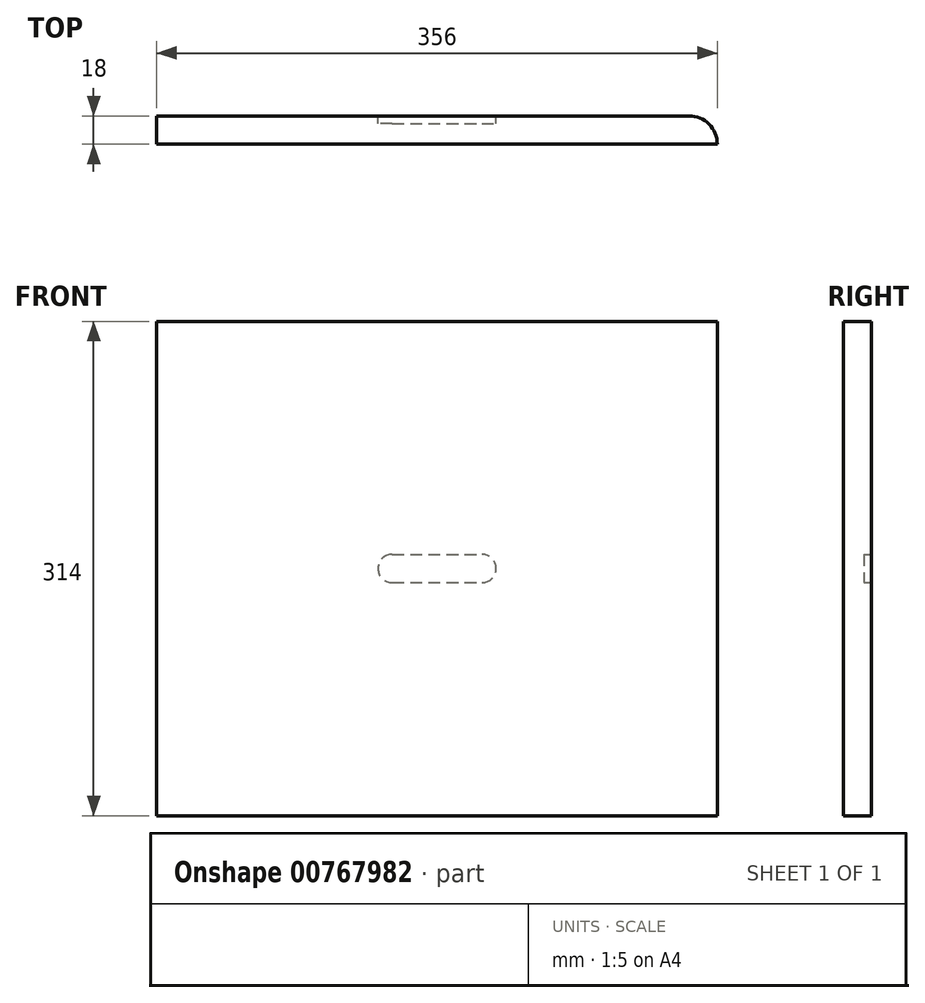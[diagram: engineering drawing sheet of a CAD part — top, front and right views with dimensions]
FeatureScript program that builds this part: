
annotation { "Feature Type Name" : "Feature", "Feature Type Description" : "" }
export const myFeature = defineFeature(function(context is Context, id is Id, definition is map)
    precondition{}
    {
        {
            var Q0;
            Q0=qCreatedBy(makeId("Front.planeOp"),FACE);
            var sketch = newSketch(context, id + "F0", { "sketchPlane" : qUnion([Q0])});
            skLineSegment(sketch, "E0.bottom", {"start": v(178, 157) * mm, "end": v(-178, 157) * mm});
            skLineSegment(sketch, "E0.top", {"start": v(178, -157) * mm, "end": v(-178, -157) * mm});
            skLineSegment(sketch, "E0.left", {"start": v(178, 157) * mm, "end": v(178, -157) * mm});
            skLineSegment(sketch, "E0.right", {"start": v(-178, 157) * mm, "end": v(-178, -157) * mm});
            skPoint(sketch, "E0.middle", {"position": v(0, 0) * mm});
            skSolve(sketch);
        }
        {
            var Q0;
            Q0 = qSketchRegion(id + "F0", true);
            extrude(context, id + "F1", {"entities" : qUnion([Q0]), "depth" : 18 * mm, "offsetDistance" : 25 * mm});
        }
        {
            var Q0;
            Q0=makeQuery(id+"F1.opExtrude","CAP_FACE",FACE,{"disambiguationData":[OSD([sQuery(id+"F0.wireOp",EDGE,"E0.bottom"),sQuery(id+"F0.wireOp",EDGE,"E0.top"),sQuery(id+"F0.wireOp",EDGE,"E0.left"),sQuery(id+"F0.wireOp",EDGE,"E0.right")])],"isStart":true});
            var sketch = newSketch(context, id + "F2", { "sketchPlane" : qUnion([Q0])});
            skLineSegment(sketch, "E1.bottom", {"start": v(28.5, 9) * mm, "end": v(-28.5, 9) * mm});
            skLineSegment(sketch, "E1.top", {"start": v(28.5, -9) * mm, "end": v(-28.5, -9) * mm});
            skLineSegment(sketch, "E1.left", {"start": v(28.5, 9) * mm, "end": v(28.5, -9) * mm, "construction": true});
            skLineSegment(sketch, "E1.right", {"start": v(-28.5, 9) * mm, "end": v(-28.5, -9) * mm, "construction": true});
            skPoint(sketch, "E1.middle", {"position": v(0, 0) * mm});
            skArc(sketch, "E2", {"start": v(-28.5, 9) * mm, "mid": v(-37.5, 0) * mm, "end": v(-28.5, -9) * mm});
            skArc(sketch, "E3", {"start": v(28.5, 9) * mm, "mid": v(37.5, 0) * mm, "end": v(28.5, -9) * mm});
            skSolve(sketch);
        }
        {
            var Q0;
            Q0 = qSketchRegion(id + "F2", true);
            extrude(context, id + "F3", {"entities" : qUnion([Q0]), "operationType" : NewBodyOperationType.REMOVE, "oppositeDirection" : true, "depth" : 5 * mm, "offsetDistance" : 25 * mm});
        }
        {
            var Q0;
            Q0=makeQuery(id+"F1.opExtrude","CAP_EDGE",EDGE,{"disambiguationData":[OSD([sQuery(id+"F0.wireOp",EDGE,"E0.left")])],"isStart":true});
            fillet(context, id + "F4", {"entities" : qUnion([Q0]), "radius" : 18 * mm, "tangentPropagation" : true, "allowEdgeOverflow" : false});
        }
    });
